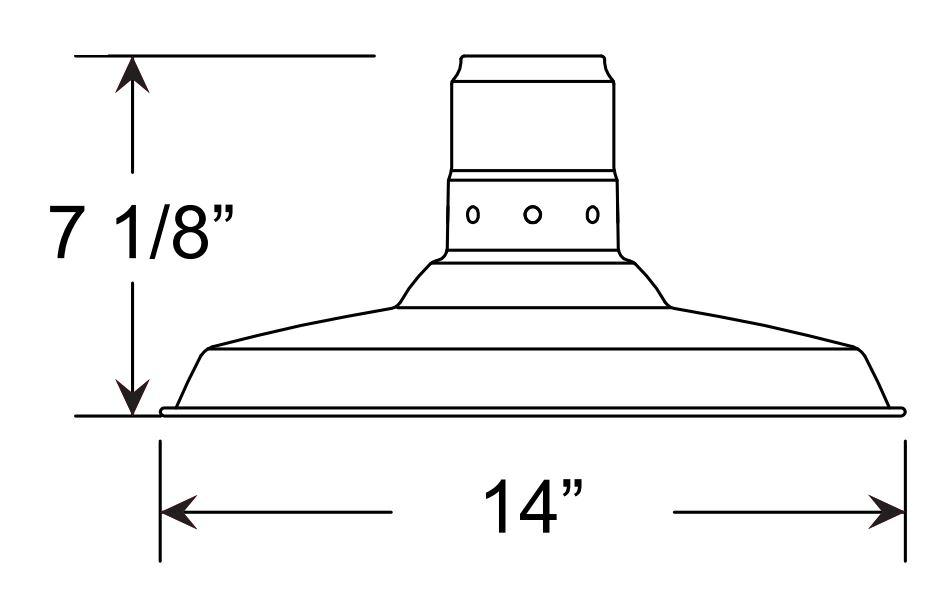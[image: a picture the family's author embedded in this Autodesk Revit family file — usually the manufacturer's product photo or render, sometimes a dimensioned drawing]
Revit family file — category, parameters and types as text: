
# Revit family: OSDDF Metal Fabric LED 22,30,36
name_source: partatom
category: Lighting Fixtures
units: mm (PartAtom-declared; Revit-internal decimal feet)

## family parameters
Always vertical = Yes
Cut with Voids When Loaded = No
Light Source = Yes
OmniClass Number = 23.80.70.00
OmniClass Title = Lighting
Part Type = Normal
Room Calculation Point = No
Round Connector Dimension = Use Diameter
Shared = No
Work Plane-Based = No

## types (3) — shared parameters
Apparent Load = 24 VA
Body Colour = Spun aluminium
Body Material = body
Bulb = Glass
CRI = >90
Canopy Body = GY
Color Filter = 16777215
Construction Material = Heavy Duty spun aluminum.
Default Elevation = 0' - 0"
Description = 120-277 Voltage
Dimming = 1%
Dimming Lamp Color Temperature Shift = <None>
Efficiency = 97-125 lumens per watt
HUB = Black
Lamp = LED
Life = L70 50,000 hours
Load Classification = Lighting
Manufacturer = ANP Lighting
Photometric Web File = generic
Power Factor = 1
Tilt Angle = 90.00°
URL = https://www.anplighting.com
Voltage = 120 V
Warranty = 5 year limited warranty
b = 0' - 3"

## per-type parameters (varying)
| type | Fixture Diameter | Fixture Height | OSDDF22 | OSDDF30 | OSDDF36 | Wattage Comments | Weight | a |
| OSDDF22 | 1' - 10" | 1' - 1" | Yes | No | No | 24 W | 9.0 lbs | 1' - 1" |
| OSDDF30 | 2' - 6" | 1' - 5 1/2" | No | Yes | No | 24W | 10.5 lbs | 1' - 6" |
| OSDDF36 | 3' - 0" | 1' - 9" | No | No | Yes | 24W | 11.5 lbs | 1' - 8" |

note: column(s) folded — value = type name in every type: Model

## geometry (parser evidence)
native form markers: Sweep x33
no freeform markers — native parametric forms only
